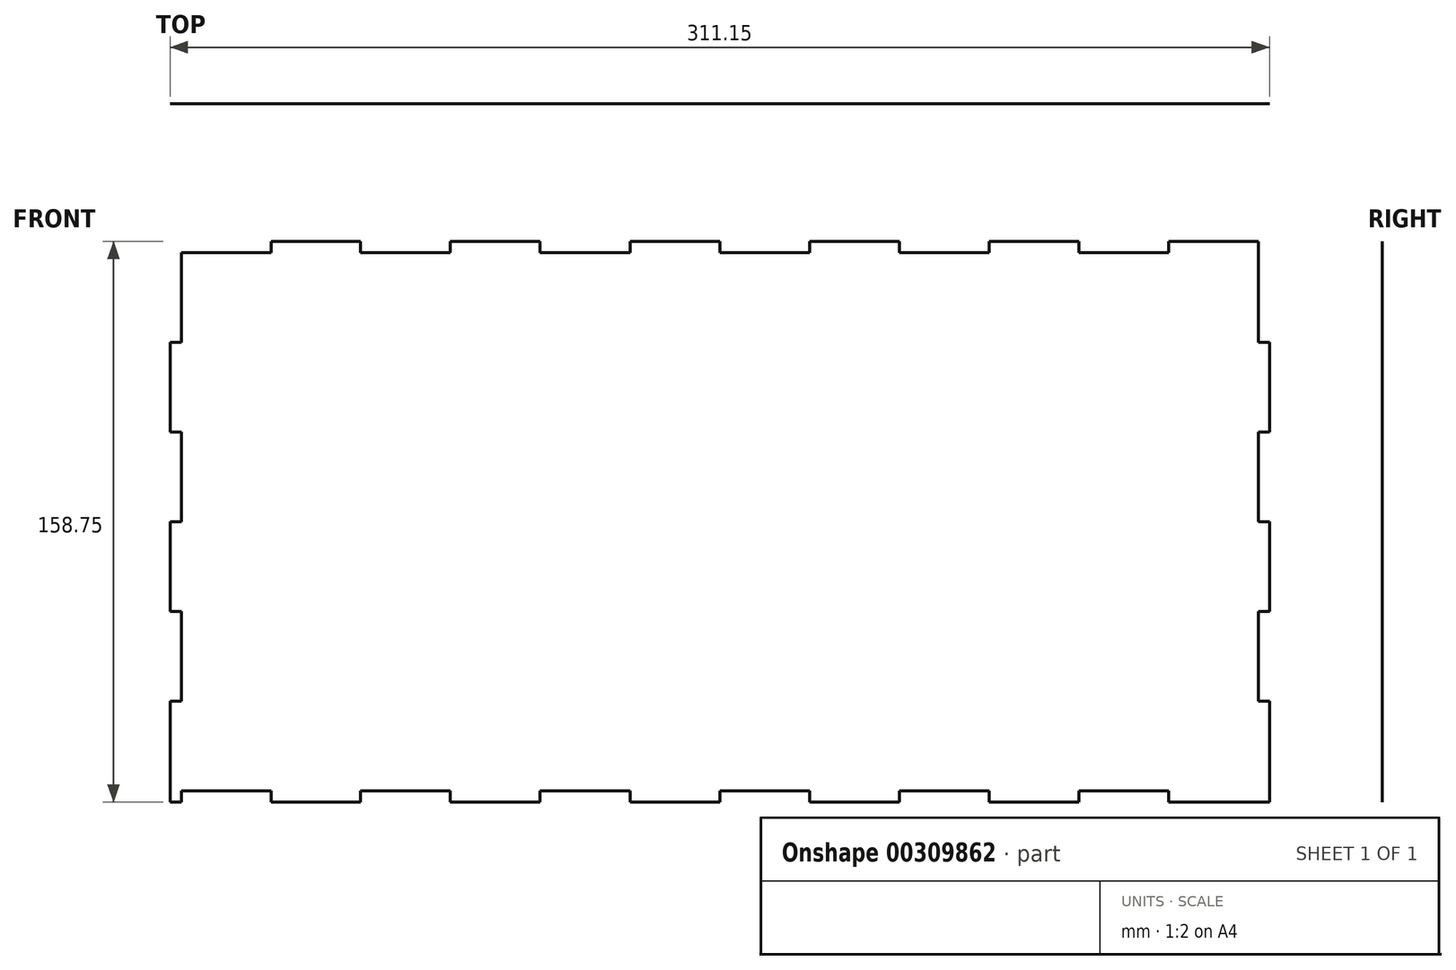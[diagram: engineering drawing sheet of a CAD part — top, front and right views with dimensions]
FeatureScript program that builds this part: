
annotation { "Feature Type Name" : "Feature", "Feature Type Description" : "" }
export const myFeature = defineFeature(function(context is Context, id is Id, definition is map)
    precondition{}
    {
        {
            var Q0;
            Q0=qCreatedBy(makeId("Front.planeOp"),FACE);
            var sketch = newSketch(context, id + "F0", { "sketchPlane" : qUnion([Q0])});
            skLineSegment(sketch, "E0.MirrorCS", {"start": v(-153.56, -44.26) * mm, "end": v(-153.56, -47.44) * mm});
            skLineSegment(sketch, "E1.MirrorCS", {"start": v(-128.16, -44.26) * mm, "end": v(-128.16, -47.44) * mm});
            skLineSegment(sketch, "E2.MirrorCS", {"start": v(-102.76, -44.26) * mm, "end": v(-102.76, -47.44) * mm});
            skLineSegment(sketch, "E3.MirrorCS", {"start": v(-77.36, -44.26) * mm, "end": v(-77.36, -47.44) * mm});
            skLineSegment(sketch, "E4.MirrorCS", {"start": v(-51.96, -44.26) * mm, "end": v(-51.96, -47.44) * mm});
            skLineSegment(sketch, "E5.MirrorCS", {"start": v(-1.16, -44.26) * mm, "end": v(-1.16, -47.44) * mm});
            skLineSegment(sketch, "E6.MirrorCS", {"start": v(-26.56, -44.26) * mm, "end": v(-26.56, -47.44) * mm});
            skLineSegment(sketch, "E7.MirrorCS", {"start": v(49.64, -44.26) * mm, "end": v(49.64, -47.44) * mm});
            skLineSegment(sketch, "E8.MirrorCS", {"start": v(24.24, -44.26) * mm, "end": v(24.24, -47.44) * mm});
            skLineSegment(sketch, "E9.MirrorCS", {"start": v(75.04, -44.26) * mm, "end": v(75.04, -47.44) * mm});
            skLineSegment(sketch, "E10", {"start": v(-178.96, -44.26) * mm, "end": v(-153.56, -44.26) * mm});
            skLineSegment(sketch, "E11", {"start": v(-128.16, -44.26) * mm, "end": v(-102.76, -44.26) * mm});
            skLineSegment(sketch, "E12", {"start": v(-102.76, -47.44) * mm, "end": v(-77.36, -47.44) * mm});
            skLineSegment(sketch, "E13", {"start": v(-77.36, -44.26) * mm, "end": v(-51.96, -44.26) * mm});
            skLineSegment(sketch, "E14", {"start": v(-51.96, -47.44) * mm, "end": v(-26.56, -47.44) * mm});
            skLineSegment(sketch, "E15", {"start": v(-26.56, -44.26) * mm, "end": v(-1.16, -44.26) * mm});
            skLineSegment(sketch, "E16", {"start": v(24.24, -44.26) * mm, "end": v(49.64, -44.26) * mm});
            skLineSegment(sketch, "E17", {"start": v(49.64, -47.44) * mm, "end": v(75.04, -47.44) * mm});
            skLineSegment(sketch, "E18", {"start": v(75.04, -44.26) * mm, "end": v(100.44, -44.26) * mm});
            skLineSegment(sketch, "E19", {"start": v(-182.14, -44.26) * mm, "end": v(-182.14, -18.86) * mm});
            skLineSegment(sketch, "E20", {"start": v(-182.14, -18.86) * mm, "end": v(-178.96, -18.86) * mm});
            skLineSegment(sketch, "E21", {"start": v(-178.96, -18.86) * mm, "end": v(-178.96, 6.54) * mm});
            skLineSegment(sketch, "E22", {"start": v(-178.96, 6.54) * mm, "end": v(-182.14, 6.54) * mm});
            skLineSegment(sketch, "E23", {"start": v(-182.14, 6.54) * mm, "end": v(-182.14, 31.94) * mm});
            skLineSegment(sketch, "E24", {"start": v(-182.14, 31.94) * mm, "end": v(-178.96, 31.94) * mm});
            skLineSegment(sketch, "E25", {"start": v(-178.96, 31.94) * mm, "end": v(-178.96, 57.34) * mm});
            skLineSegment(sketch, "E26", {"start": v(-178.96, 57.34) * mm, "end": v(-182.14, 57.34) * mm});
            skLineSegment(sketch, "E27", {"start": v(-182.14, 57.34) * mm, "end": v(-182.14, 82.74) * mm});
            skLineSegment(sketch, "E28", {"start": v(-182.14, 82.74) * mm, "end": v(-178.96, 82.74) * mm});
            skLineSegment(sketch, "E29", {"start": v(-178.96, 82.74) * mm, "end": v(-178.96, 108.14) * mm});
            skLineSegment(sketch, "E30", {"start": v(-178.96, 108.14) * mm, "end": v(-153.56, 108.14) * mm});
            skLineSegment(sketch, "E31", {"start": v(125.84, 108.14) * mm, "end": v(125.84, 82.74) * mm});
            skLineSegment(sketch, "E32", {"start": v(-1.16, -47.44) * mm, "end": v(24.24, -47.44) * mm});
            skLineSegment(sketch, "E33", {"start": v(-26.56, 108.14) * mm, "end": v(-26.56, -44.26) * mm});
            skLineSegment(sketch, "E34", {"start": v(-153.56, -47.44) * mm, "end": v(-128.16, -47.44) * mm});
            skLineSegment(sketch, "E35", {"start": v(125.84, -47.44) * mm, "end": v(100.44, -47.44) * mm});
            skLineSegment(sketch, "E36", {"start": v(100.44, -47.44) * mm, "end": v(100.44, -44.26) * mm});
            skLineSegment(sketch, "E37.MirrorCS", {"start": v(-153.56, 111.31) * mm, "end": v(-128.16, 111.31) * mm});
            skLineSegment(sketch, "E38.MirrorCS", {"start": v(-102.76, 111.31) * mm, "end": v(-77.36, 111.31) * mm});
            skLineSegment(sketch, "E39.MirrorCS", {"start": v(-51.96, 111.31) * mm, "end": v(-26.56, 111.31) * mm});
            skLineSegment(sketch, "E40.MirrorCS", {"start": v(-1.16, 111.31) * mm, "end": v(24.24, 111.31) * mm});
            skLineSegment(sketch, "E41.MirrorCS", {"start": v(49.64, 111.31) * mm, "end": v(75.04, 111.31) * mm});
            skLineSegment(sketch, "E42.MirrorCS", {"start": v(125.84, 111.31) * mm, "end": v(100.44, 111.31) * mm});
            skLineSegment(sketch, "E43.MirrorCS", {"start": v(-153.56, 108.14) * mm, "end": v(-153.56, 111.31) * mm});
            skLineSegment(sketch, "E44.MirrorCS", {"start": v(-128.16, 108.14) * mm, "end": v(-128.16, 111.31) * mm});
            skLineSegment(sketch, "E45.MirrorCS", {"start": v(-102.76, 108.14) * mm, "end": v(-102.76, 111.31) * mm});
            skLineSegment(sketch, "E46.MirrorCS", {"start": v(-51.96, 108.14) * mm, "end": v(-51.96, 111.31) * mm});
            skLineSegment(sketch, "E47.MirrorCS", {"start": v(-77.36, 108.14) * mm, "end": v(-77.36, 111.31) * mm});
            skLineSegment(sketch, "E48.MirrorCS", {"start": v(100.44, 111.31) * mm, "end": v(100.44, 108.14) * mm});
            skLineSegment(sketch, "E49.MirrorCS", {"start": v(75.04, 108.14) * mm, "end": v(75.04, 111.31) * mm});
            skLineSegment(sketch, "E50.MirrorCS", {"start": v(49.64, 108.14) * mm, "end": v(49.64, 111.31) * mm});
            skLineSegment(sketch, "E51.MirrorCS", {"start": v(24.24, 108.14) * mm, "end": v(24.24, 111.31) * mm});
            skLineSegment(sketch, "E52.MirrorCS", {"start": v(-26.56, 108.14) * mm, "end": v(-26.56, 111.31) * mm});
            skLineSegment(sketch, "E53.MirrorCS", {"start": v(-1.16, 108.14) * mm, "end": v(-1.16, 111.31) * mm});
            skLineSegment(sketch, "E54.trimOffspring", {"start": v(-128.16, 108.14) * mm, "end": v(-102.76, 108.14) * mm});
            skLineSegment(sketch, "E55.trimOffspring", {"start": v(-77.36, 108.14) * mm, "end": v(-51.96, 108.14) * mm});
            skLineSegment(sketch, "E56.trimOffspring", {"start": v(-26.56, 108.14) * mm, "end": v(-1.16, 108.14) * mm});
            skLineSegment(sketch, "E57.trimOffspring", {"start": v(24.24, 108.14) * mm, "end": v(49.64, 108.14) * mm});
            skLineSegment(sketch, "E58.trimOffspring", {"start": v(75.04, 108.14) * mm, "end": v(100.44, 108.14) * mm});
            skLineSegment(sketch, "E59.MirrorCS", {"start": v(129.01, 57.34) * mm, "end": v(129.01, 82.74) * mm});
            skLineSegment(sketch, "E60.MirrorCS", {"start": v(129.01, 6.54) * mm, "end": v(129.01, 31.94) * mm});
            skLineSegment(sketch, "E61.MirrorCS", {"start": v(129.01, -44.26) * mm, "end": v(129.01, -18.86) * mm});
            skLineSegment(sketch, "E62", {"start": v(129.01, -18.86) * mm, "end": v(125.84, -18.86) * mm});
            skLineSegment(sketch, "E63", {"start": v(129.01, 6.54) * mm, "end": v(125.84, 6.54) * mm});
            skLineSegment(sketch, "E64", {"start": v(129.01, 31.94) * mm, "end": v(125.84, 31.94) * mm});
            skLineSegment(sketch, "E65", {"start": v(125.84, 111.31) * mm, "end": v(125.84, 108.14) * mm});
            skLineSegment(sketch, "E66", {"start": v(129.01, 82.74) * mm, "end": v(125.84, 82.74) * mm});
            skLineSegment(sketch, "E67", {"start": v(129.01, 57.34) * mm, "end": v(125.84, 57.34) * mm});
            skLineSegment(sketch, "E68.trimOffspring", {"start": v(125.84, 57.34) * mm, "end": v(125.84, 31.94) * mm});
            skLineSegment(sketch, "E69.trimOffspring", {"start": v(125.84, 6.54) * mm, "end": v(125.84, -18.86) * mm});
            skLineSegment(sketch, "E70", {"start": v(125.84, -47.44) * mm, "end": v(129.01, -47.44) * mm});
            skLineSegment(sketch, "E71", {"start": v(129.01, -47.44) * mm, "end": v(129.01, -44.26) * mm});
            skPoint(sketch, "E72.end.orphan", {"position": v(125.84, -44.26) * mm});
            skLineSegment(sketch, "E73", {"start": v(-182.14, -44.26) * mm, "end": v(-182.14, -47.44) * mm});
            skLineSegment(sketch, "E74", {"start": v(-182.14, -47.44) * mm, "end": v(-178.96, -47.44) * mm});
            skLineSegment(sketch, "E75", {"start": v(-178.96, -47.44) * mm, "end": v(-178.96, -44.26) * mm});
            skSolve(sketch);
        }
        {
            var Q0;
            Q0=makeQuery(id+"F0.imprint","IMPRINT",FACE,{"disambiguationData":[TD([[makeQuery(id+"F0.imprint","IMPRINT",EDGE,{"derivedFrom":sQuery(id+"F0.wireOp",EDGE,"E0.MirrorCS")}),1.0]])]});
            var Q1;
            Q1=makeQuery(id+"F0.imprint","IMPRINT",FACE,{"disambiguationData":[TD([[makeQuery(id+"F0.imprint","IMPRINT",EDGE,{"derivedFrom":sQuery(id+"F0.wireOp",EDGE,"E5.MirrorCS")}),1.0]])]});
            extrude(context, id + "F1", {"entities" : qUnion([Q0, Q1]), "depth" : 1 / 203.2 * mm});
        }
    });
